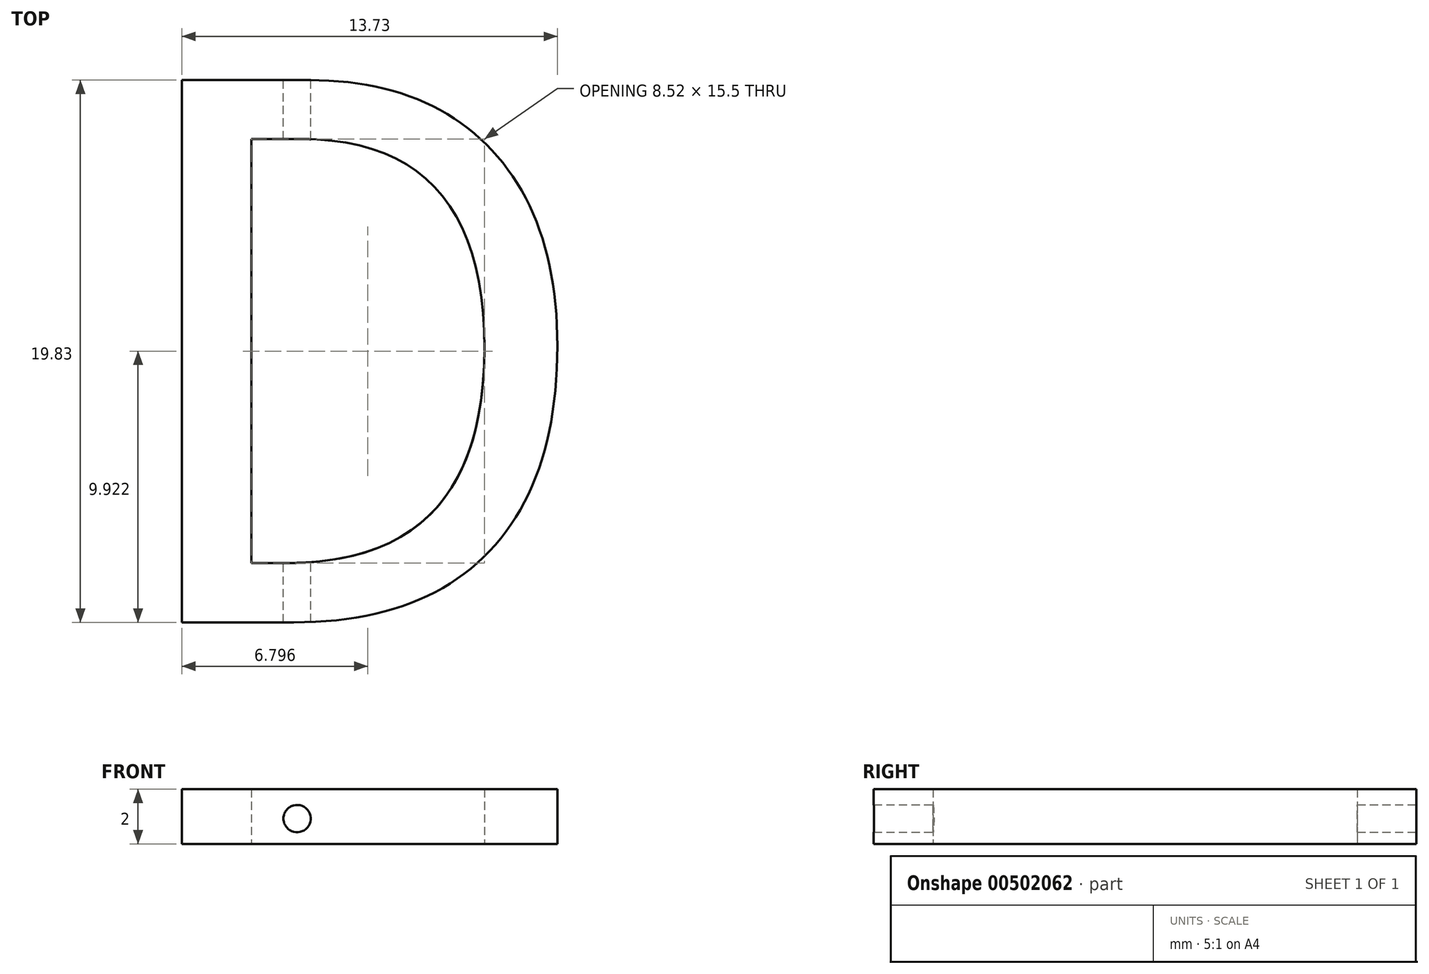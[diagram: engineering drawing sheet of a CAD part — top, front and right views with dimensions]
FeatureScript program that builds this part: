
annotation { "Feature Type Name" : "Feature", "Feature Type Description" : "" }
export const myFeature = defineFeature(function(context is Context, id is Id, definition is map)
    precondition{}
    {
        {
            var Q0;
            Q0=qCreatedBy(makeId("Top.planeOp"),FACE);
            var sketch = newSketch(context, id + "F0", { "sketchPlane" : qUnion([Q0])});
            skText(sketch, "E0", { "text": "D", "fontName": "DroidSansMono.ttf"});
            const initialGuessF0  = {"E0": [-0.01972, 0, 1, 0, 0.02]};
            skSetInitialGuess(sketch, initialGuessF0);
            skSolve(sketch);
        }
        {
            var Q0;
            Q0=makeQuery(id+"F0.imprint","IMPRINT",FACE,{"disambiguationData":[TD([[makeQuery(id+"F0.imprint","IMPRINT",EDGE,{"derivedFrom":sQuery(id+"F0.wireOp",EDGE,"E0.sketch_text.stroke-0")}),-1.0]])]});
            extrude(context, id + "F1", {"entities" : qUnion([Q0]), "depth" : 2 * mm});
        }
        {
            var Q0;
            Q0=makeQuery(id+"F1.opExtrude","SWEPT_FACE",FACE,{"disambiguationData":[OSD([sQuery(id+"F0.wireOp",EDGE,"E0.sketch_text.stroke-1")])]});
            var sketch = newSketch(context, id + "F2", { "sketchPlane" : qUnion([Q0])});
            skCircle(sketch, "E1", {"center": v(13.68, 0.92) * mm, "radius": 0.5 * mm});
            skSolve(sketch);
        }
        {
            var Q0;
            Q0 = qSketchRegion(id + "F2", true);
            extrude(context, id + "F3", {"entities" : qUnion([Q0]), "operationType" : NewBodyOperationType.REMOVE, "oppositeDirection" : true, "depth" : 50 * mm});
        }
    });
